# Revit family: Поли-Групп_ЗадвижкаКлиноваяEAZ-EК-F4_DN40-900
name_source: partatom
category: Арматура трубопроводов
units: mm (PartAtom-declared; Revit-internal decimal feet)

## family parameters
Всегда вертикально = Да
На основе рабочей плоскости = Нет
Общий = Нет
При загрузке вырезать с полостями = Нет
Размер круглого соединителя = Использовать диаметр
Тип детали = Клапан - Вставляется

## types (29) — shared parameters
ADSK_URL страницы изделия = https://www.polycorr.ru
ADSK_Версия Revit = 2019
ADSK_Единица измерения = шт
ADSK_Завод-изготовитель = ООО ПК «Поли-Групп»
ADSK_Количество = 1
ADSK_Материал = Высокопрочный чугун GGG-40
ADSK_Материал наименование = Высокопрочный чугун с шаровидным графитом (GGG-40)
Класс герметичности = А по ГОСТ Р 9544-2015
Материал Диска = Высокопрочный чугун с шаровидным графитом (GGG-40)
Материал уплотнителя = EPDM/NBR
Назначение = Для установки в качестве запорного устройства на трубопроводах
Покрытие = Высококачественное эпоксидное покрытие толщиной 300 мкм
Рабочая среда = Питьевая вода, техническая вода, канализационные стоки, морская вода
Разработчик = https://3dbim.pro
Срок службы = 50 лет
ТВ = Поли-Групп_ЗадвижкаКлиноваяEAZ-EК-F4_DN40-900
Температура рабочей среды = 0 до +70°С
Тип привода = Штурвал
Тип присоединения = Фланцевое

## per-type parameters (varying)
- 40-16: A=135 мм; ADSK_Марка=EAZ-GV-4-F4 DN40 PN16; ADSK_Масса=8.2; ADSK_Масса_Текст=8.2; ADSK_Наименование=Задвижка с обрезиненным клином EAZ EK F4 для воды с мягким уплотнением фланцевая маховик DN40 PN16; ADSK_Наименование краткое=Задвижка клиновая EAZ EK F4 DN40 PN16; D=150 мм; D2=88 мм; DN=40 мм; DO=160 мм; D_Наружный=49 мм; H2=240 мм; Kv=0.2 м³/ч; L=140 мм; PN=16.0 бары; R=10 мм; b=19 мм; d1=10 мм; f=3 мм; h2=120 мм; l1=84 мм; l2=91 мм; l3=126 мм; t=12 мм; Габаритные размеры=150х140х315
- 50-16: A=149 мм; ADSK_Марка=EAZ-GV-4-F4 DN50 PN16; ADSK_Масса=9.2; ADSK_Масса_Текст=9.2; ADSK_Наименование=Задвижка с обрезиненным клином EAZ EK F4 для воды с мягким уплотнением фланцевая маховик DN50 PN16; ADSK_Наименование краткое=Задвижка клиновая EAZ EK F4 DN50 PN16; D=165 мм; D2=100 мм; DN=50 мм; DO=160 мм; D_Наружный=59 мм; H2=240 мм; Kv=0.2 м³/ч; L=150 мм; PN=16.0 бары; R=10 мм; b=19 мм; d1=13 мм; f=3 мм; h2=120 мм; l1=90 мм; l2=98 мм; l3=135 мм; t=12 мм; Габаритные размеры=165х150х323
- 65-16: A=167 мм; ADSK_Марка=EAZ-GV-4-F4 DN65 PN16; ADSK_Масса=12; ADSK_Масса_Текст=12; ADSK_Наименование=Задвижка с обрезиненным клином EAZ EK F4 для воды с мягким уплотнением фланцевая маховик DN65 PN16; ADSK_Наименование краткое=Задвижка клиновая EAZ EK F4 DN65 PN16; D=185 мм; D2=120 мм; DN=65 мм; DO=160 мм; D_Наружный=74 мм; H2=259 мм; Kv=0.2 м³/ч; L=170 мм; PN=16.0 бары; R=10 мм; b=19 мм; d1=16 мм; f=3 мм; h2=130 мм; l1=102 мм; l2=111 мм; l3=153 мм; t=13 мм; Габаритные размеры=185х170х352
- 80-16: A=180 мм; ADSK_Марка=EAZ-GV-4-F4 DN80 PN16; ADSK_Масса=14; ADSK_Масса_Текст=14; ADSK_Наименование=Задвижка с обрезиненным клином EAZ EK F4 для воды с мягким уплотнением фланцевая маховик DN80 PN16; ADSK_Наименование краткое=Задвижка клиновая EAZ EK F4 DN80 PN16; D=200 мм; D2=135 мм; DN=80 мм; DO=200 мм; D_Наружный=89 мм; H2=295 мм; Kv=0.1 м³/ч; L=180 мм; PN=16.0 бары; R=10 мм; b=19 мм; d1=20 мм; f=3 мм; h2=148 мм; l1=108 мм; l2=117 мм; l3=162 мм; t=15 мм; Габаритные размеры=200х180х395
- 100-16: A=198 мм; ADSK_Марка=EAZ-GV-4-F4 DN100 PN16; ADSK_Масса=18; ADSK_Масса_Текст=18; ADSK_Наименование=Задвижка с обрезиненным клином EAZ EK F4 для воды с мягким уплотнением фланцевая маховик DN100 PN16; ADSK_Наименование краткое=Задвижка клиновая EAZ EK F4 DN100 PN16; D=220 мм; D2=156 мм; DN=100 мм; DO=200 мм; D_Наружный=109 мм; H2=327 мм; Kv=0.1 м³/ч; L=190 мм; PN=16.0 бары; R=11 мм; b=19 мм; d1=25 мм; f=3 мм; h2=164 мм; l1=114 мм; l2=124 мм; l3=171 мм; t=16 мм; Габаритные размеры=220х190х437
- 125-16: A=225 мм; ADSK_Марка=EAZ-GV-4-F4 DN125 PN16; ADSK_Масса=24; ADSK_Масса_Текст=24; ADSK_Наименование=Задвижка с обрезиненным клином EAZ EK F4 для воды с мягким уплотнением фланцевая маховик DN125 PN16; ADSK_Наименование краткое=Задвижка клиновая EAZ EK F4 DN125 PN16; D=250 мм; D2=186 мм; DN=125 мм; DO=250 мм; D_Наружный=134 мм; H2=388 мм; Kv=0.1 м³/ч; L=200 мм; PN=16.0 бары; R=11 мм; b=19 мм; d1=31 мм; f=3 мм; h2=194 мм; l1=120 мм; l2=130 мм; l3=180 мм; t=19 мм; Габаритные размеры=250х200х513
- 150-16: A=257 мм; ADSK_Марка=EAZ-GV-4-F4 DN150 PN16; ADSK_Масса=31; ADSK_Масса_Текст=31; ADSK_Наименование=Задвижка с обрезиненным клином EAZ EK F4 для воды с мягким уплотнением фланцевая маховик DN150 PN16; ADSK_Наименование краткое=Задвижка клиновая EAZ EK F4 DN150 PN16; D=285 мм; D2=212 мм; DN=150 мм; DO=250 мм; D_Наружный=159 мм; H2=431 мм; Kv=0.1 м³/ч; L=210 мм; PN=16.0 бары; R=11 мм; b=19 мм; d1=38 мм; f=3 мм; h2=216 мм; l1=126 мм; l2=137 мм; l3=189 мм; t=22 мм; Габаритные размеры=285х210х574
- 200-16: A=306 мм; ADSK_Марка=EAZ-GV-4-F4 DN200 PN16; ADSK_Масса=50; ADSK_Масса_Текст=50; ADSK_Наименование=Задвижка с обрезиненным клином EAZ EK F4 для воды с мягким уплотнением фланцевая маховик DN200 PN16; ADSK_Наименование краткое=Задвижка клиновая EAZ EK F4 DN200 PN16; D=340 мм; D2=268 мм; DN=200 мм; DO=280 мм; D_Наружный=209 мм; H2=527 мм; Kv=0.1 м³/ч; L=230 мм; PN=16.0 бары; R=13 мм; b=20 мм; d1=50 мм; f=3 мм; h2=264 мм; l1=138 мм; l2=150 мм; l3=207 мм; t=26 мм; Габаритные размеры=340х230х697
- 250-16: A=365 мм; ADSK_Марка=EAZ-GV-4-F4 DN250 PN16; ADSK_Масса=77; ADSK_Масса_Текст=77; ADSK_Наименование=Задвижка с обрезиненным клином EAZ EK F4 для воды с мягким уплотнением фланцевая маховик DN250 PN16; ADSK_Наименование краткое=Задвижка клиновая EAZ EK F4 DN250 PN16; D=405 мм; D2=318 мм; DN=250 мм; DO=320 мм; D_Наружный=259 мм; H2=609 мм; Kv=0.1 м³/ч; L=250 мм; PN=16.0 бары; R=15 мм; b=22 мм; d1=63 мм; f=3 мм; h2=305 мм; l1=150 мм; l2=163 мм; l3=225 мм; t=30 мм; Габаритные размеры=405х250х812
- 300-16: A=414 мм; ADSK_Марка=EAZ-GV-4-F4 DN300 PN16; ADSK_Масса=107; ADSK_Масса_Текст=107; ADSK_Наименование=Задвижка с обрезиненным клином EAZ EK F4 для воды с мягким уплотнением фланцевая маховик DN300 PN16; ADSK_Наименование краткое=Задвижка клиновая EAZ EK F4 DN300 PN16; D=460 мм; D2=373 мм; DN=300 мм; DO=350 мм; D_Наружный=309 мм; H2=698 мм; Kv=0.1 м³/ч; L=270 мм; PN=16.0 бары; R=17 мм; b=25 мм; d1=75 мм; f=3 мм; h2=349 мм; l1=162 мм; l2=176 мм; l3=243 мм; t=35 мм; Габаритные размеры=460х270х928
- 350-16: A=468 мм; ADSK_Марка=EAZ-GV-4-F4 DN350 PN16; ADSK_Масса=183; ADSK_Масса_Текст=183; ADSK_Наименование=Задвижка с обрезиненным клином EAZ EK F4 для воды с мягким уплотнением фланцевая маховик DN350 PN16; ADSK_Наименование краткое=Задвижка клиновая EAZ EK F4 DN350 PN16; D=520 мм; D2=433 мм; DN=350 мм; DO=400 мм; D_Наружный=359 мм; H2=796 мм; Kv=0.0 м³/ч; L=290 мм; PN=16.0 бары; R=21 мм; b=27 мм; d1=88 мм; f=3 мм; h2=398 мм; l1=174 мм; l2=189 мм; l3=261 мм; t=40 мм; Габаритные размеры=520х290х1056
- 400-16: A=522 мм; ADSK_Марка=EAZ-GV-4-F4 DN400 PN16; ADSK_Масса=228; ADSK_Масса_Текст=228; ADSK_Наименование=Задвижка с обрезиненным клином EAZ EK F4 для воды с мягким уплотнением фланцевая маховик DN400 PN16; ADSK_Наименование краткое=Задвижка клиновая EAZ EK F4 DN400 PN16; D=580 мм; D2=483 мм; DN=400 мм; DO=500 мм; D_Наружный=409 мм; H2=943 мм; Kv=0.0 м³/ч; L=310 мм; PN=16.0 бары; R=21 мм; b=28 мм; d1=100 мм; f=4 мм; h2=472 мм; l1=186 мм; l2=202 мм; l3=279 мм; t=47 мм; Габаритные размеры=580х310х1233
- 450-16: A=576 мм; ADSK_Марка=EAZ-GV-4-F4 DN450 PN16; ADSK_Масса=320; ADSK_Масса_Текст=320; ADSK_Наименование=Задвижка с обрезиненным клином EAZ EK F4 для воды с мягким уплотнением фланцевая маховик DN450 PN16; ADSK_Наименование краткое=Задвижка клиновая EAZ EK F4 DN450 PN16; D=640 мм; D2=546 мм; DN=450 мм; DO=500 мм; D_Наружный=459 мм; H2=1032 мм; Kv=0.0 м³/ч; L=330 мм; PN=16.0 бары; R=28 мм; b=30 мм; d1=113 мм; f=4 мм; h2=516 мм; l1=198 мм; l2=215 мм; l3=297 мм; t=52 мм; Габаритные размеры=640х330х1352
- 500-16: A=644 мм; ADSK_Марка=EAZ-GV-4-F4 DN500 PN16; ADSK_Масса=394; ADSK_Масса_Текст=394; ADSK_Наименование=Задвижка с обрезиненным клином EAZ EK F4 для воды с мягким уплотнением фланцевая маховик DN500 PN16; ADSK_Наименование краткое=Задвижка клиновая EAZ EK F4 DN500 PN16; D=715 мм; D2=605 мм; DN=500 мм; DO=500 мм; D_Наружный=509 мм; H2=1114 мм; Kv=1.0 м³/ч; L=350 мм; PN=16.0 бары; R=28 мм; b=32 мм; d1=125 мм; f=4 мм; h2=557 мм; l1=210 мм; l2=228 мм; l3=315 мм; t=56 мм; Габаритные размеры=715х350х1472
- 600-16: A=756 мм; ADSK_Марка=EAZ-GV-4-F4 DN600 PN16; ADSK_Масса=580; ADSK_Масса_Текст=580; ADSK_Наименование=Задвижка с обрезиненным клином EAZ EK F4 для воды с мягким уплотнением фланцевая маховик DN600 PN16; ADSK_Наименование краткое=Задвижка клиновая EAZ EK F4 DN600 PN16; D=840 мм; D2=710 мм; DN=600 мм; DO=600 мм; D_Наружный=609 мм; H2=1259 мм; Kv=1.0 м³/ч; L=390 мм; PN=16.0 бары; R=28 мм; b=36 мм; d1=150 мм; f=5 мм; h2=630 мм; l1=234 мм; l2=254 мм; l3=351 мм; t=63 мм; Габаритные размеры=840х390х1679
- 700-16: A=819 мм; ADSK_Марка=EAZ-GV-4-F4 DN700 PN16; ADSK_Масса=1050; ADSK_Масса_Текст=1050; ADSK_Наименование=Задвижка с обрезиненным клином EAZ EK F4 для воды с мягким уплотнением фланцевая маховик DN700 PN16; ADSK_Наименование краткое=Задвижка клиновая EAZ EK F4 DN700 PN16; D=910 мм; D2=797 мм; DN=700 мм; DO=700 мм; D_Наружный=709 мм; H2=1492 мм; Kv=1.0 м³/ч; L=430 мм; PN=16.0 бары; R=31 мм; b=40 мм; d1=175 мм; f=5 мм; h2=746 мм; l1=258 мм; l2=280 мм; l3=387 мм; t=75 мм; Габаритные размеры=910х430х1947
- 800-16: A=923 мм; ADSK_Марка=EAZ-GV-4-F4 DN800 PN16; ADSK_Масса=1250; ADSK_Масса_Текст=1250; ADSK_Наименование=Задвижка с обрезиненным клином EAZ EK F4 для воды с мягким уплотнением фланцевая маховик DN800 PN16; ADSK_Наименование краткое=Задвижка клиновая EAZ EK F4 DN800 PN16; D=1025 мм; D2=909 мм; DN=800 мм; DO=800 мм; D_Наружный=809 мм; H2=1630 мм; Kv=1.0 м³/ч; L=470 мм; PN=16.0 бары; R=33 мм; b=43 мм; d1=200 мм; f=5 мм; h2=815 мм; l1=282 мм; l2=306 мм; l3=423 мм; t=82 мм; Габаритные размеры=1025х470х2143
- 900-16: A=1004 мм; ADSK_Марка=EAZ-GV-4-F4 DN900 PN16; ADSK_Масса=1980; ADSK_Масса_Текст=1980; ADSK_Наименование=Задвижка с обрезиненным клином EAZ EK F4 для воды с мягким уплотнением фланцевая маховик DN900 PN16; ADSK_Наименование краткое=Задвижка клиновая EAZ EK F4 DN900 PN16; D=1115 мм; D2=1001 мм; DN=900 мм; DO=800 мм; D_Наружный=909 мм; H2=2018 мм; Kv=1.0 м³/ч; L=510 мм; PN=16.0 бары; R=37 мм; b=47 мм; d1=225 мм; f=5 мм; h2=1009 мм; l1=306 мм; l2=332 мм; l3=459 мм; t=101 мм; Габаритные размеры=1115х510х2576
- 200-10: A=306 мм; ADSK_Марка=EAZ-GV-4-F4 DN200 PN10; ADSK_Масса=50; ADSK_Масса_Текст=50; ADSK_Наименование=Задвижка с обрезиненным клином EAZ EK F4 для воды с мягким уплотнением фланцевая маховик DN200 PN10; ADSK_Наименование краткое=Задвижка клиновая EAZ EK F4 DN200 PN10; D=340 мм; D2=268 мм; DN=200 мм; DO=280 мм; D_Наружный=209 мм; H2=527 мм; Kv=0.1 м³/ч; L=230 мм; PN=10.0 бары; R=13 мм; b=20 мм; d1=50 мм; f=3 мм; h2=264 мм; l1=138 мм; l2=150 мм; l3=207 мм; t=26 мм; Габаритные размеры=340х230х697
- 250-10: A=365 мм; ADSK_Марка=EAZ-GV-4-F4 DN250 PN10; ADSK_Масса=77; ADSK_Масса_Текст=77; ADSK_Наименование=Задвижка с обрезиненным клином EAZ EK F4 для воды с мягким уплотнением фланцевая маховик DN250 PN10; ADSK_Наименование краткое=Задвижка клиновая EAZ EK F4 DN250 PN10; D=405 мм; D2=318 мм; DN=250 мм; DO=320 мм; D_Наружный=259 мм; H2=609 мм; Kv=0.1 м³/ч; L=250 мм; PN=10.0 бары; R=15 мм; b=22 мм; d1=63 мм; f=3 мм; h2=305 мм; l1=150 мм; l2=163 мм; l3=225 мм; t=30 мм; Габаритные размеры=405х250х812
- 300-10: A=414 мм; ADSK_Марка=EAZ-GV-4-F4 DN300 PN10; ADSK_Масса=107; ADSK_Масса_Текст=107; ADSK_Наименование=Задвижка с обрезиненным клином EAZ EK F4 для воды с мягким уплотнением фланцевая маховик DN300 PN10; ADSK_Наименование краткое=Задвижка клиновая EAZ EK F4 DN300 PN10; D=460 мм; D2=370 мм; DN=300 мм; DO=350 мм; D_Наружный=309 мм; H2=698 мм; Kv=0.1 м³/ч; L=270 мм; PN=10.0 бары; R=17 мм; b=25 мм; d1=75 мм; f=3 мм; h2=349 мм; l1=162 мм; l2=176 мм; l3=243 мм; t=35 мм; Габаритные размеры=460х270х928
- 350-10: A=468 мм; ADSK_Марка=EAZ-GV-4-F4 DN350 PN10; ADSK_Масса=183; ADSK_Масса_Текст=183; ADSK_Наименование=Задвижка с обрезиненным клином EAZ EK F4 для воды с мягким уплотнением фланцевая маховик DN350 PN10; ADSK_Наименование краткое=Задвижка клиновая EAZ EK F4 DN350 PN10; D=520 мм; D2=430 мм; DN=350 мм; DO=400 мм; D_Наружный=359 мм; H2=796 мм; Kv=0.0 м³/ч; L=290 мм; PN=10.0 бары; R=21 мм; b=27 мм; d1=88 мм; f=3 мм; h2=398 мм; l1=174 мм; l2=189 мм; l3=261 мм; t=40 мм; Габаритные размеры=520х290х1056
- 400-10: A=522 мм; ADSK_Марка=EAZ-GV-4-F4 DN400 PN10; ADSK_Масса=228; ADSK_Масса_Текст=228; ADSK_Наименование=Задвижка с обрезиненным клином EAZ EK F4 для воды с мягким уплотнением фланцевая маховик DN400 PN10; ADSK_Наименование краткое=Задвижка клиновая EAZ EK F4 DN400 PN10; D=580 мм; D2=480 мм; DN=400 мм; DO=500 мм; D_Наружный=409 мм; H2=943 мм; Kv=0.0 м³/ч; L=310 мм; PN=10.0 бары; R=21 мм; b=28 мм; d1=100 мм; f=4 мм; h2=472 мм; l1=186 мм; l2=202 мм; l3=279 мм; t=47 мм; Габаритные размеры=580х310х1233
- 450-10: A=576 мм; ADSK_Марка=EAZ-GV-4-F4 DN450 PN10; ADSK_Масса=320; ADSK_Масса_Текст=320; ADSK_Наименование=Задвижка с обрезиненным клином EAZ EK F4 для воды с мягким уплотнением фланцевая маховик DN450 PN10; ADSK_Наименование краткое=Задвижка клиновая EAZ EK F4 DN450 PN10; D=640 мм; D2=528 мм; DN=450 мм; DO=500 мм; D_Наружный=459 мм; H2=1032 мм; Kv=0.0 м³/ч; L=330 мм; PN=10.0 бары; R=28 мм; b=30 мм; d1=113 мм; f=4 мм; h2=516 мм; l1=198 мм; l2=215 мм; l3=297 мм; t=52 мм; Габаритные размеры=640х330х1352
- 500-10: A=644 мм; ADSK_Марка=EAZ-GV-4-F4 DN500 PN10; ADSK_Масса=394; ADSK_Масса_Текст=394; ADSK_Наименование=Задвижка с обрезиненным клином EAZ EK F4 для воды с мягким уплотнением фланцевая маховик DN500 PN10; ADSK_Наименование краткое=Задвижка клиновая EAZ EK F4 DN500 PN10; D=715 мм; D2=582 мм; DN=500 мм; DO=500 мм; D_Наружный=509 мм; H2=1114 мм; Kv=1.0 м³/ч; L=350 мм; PN=10.0 бары; R=28 мм; b=32 мм; d1=125 мм; f=4 мм; h2=557 мм; l1=210 мм; l2=228 мм; l3=315 мм; t=56 мм; Габаритные размеры=715х350х1472
- 600-10: A=756 мм; ADSK_Марка=EAZ-GV-4-F4 DN600 PN10; ADSK_Масса=580; ADSK_Масса_Текст=580; ADSK_Наименование=Задвижка с обрезиненным клином EAZ EK F4 для воды с мягким уплотнением фланцевая маховик DN600 PN10; ADSK_Наименование краткое=Задвижка клиновая EAZ EK F4 DN600 PN10; D=840 мм; D2=680 мм; DN=600 мм; DO=600 мм; D_Наружный=609 мм; H2=1259 мм; Kv=1.0 м³/ч; L=390 мм; PN=10.0 бары; R=28 мм; b=36 мм; d1=150 мм; f=5 мм; h2=630 мм; l1=234 мм; l2=254 мм; l3=351 мм; t=63 мм; Габаритные размеры=840х390х1679
- 700-10: A=819 мм; ADSK_Марка=EAZ-GV-4-F4 DN700 PN10; ADSK_Масса=1050; ADSK_Масса_Текст=1050; ADSK_Наименование=Задвижка с обрезиненным клином EAZ EK F4 для воды с мягким уплотнением фланцевая маховик DN700 PN10; ADSK_Наименование краткое=Задвижка клиновая EAZ EK F4 DN700 PN10; D=910 мм; D2=797 мм; DN=700 мм; DO=700 мм; D_Наружный=709 мм; H2=1492 мм; Kv=1.0 м³/ч; L=430 мм; PN=10.0 бары; R=31 мм; b=40 мм; d1=175 мм; f=5 мм; h2=746 мм; l1=258 мм; l2=280 мм; l3=387 мм; t=75 мм; Габаритные размеры=910х430х1947
- 800-10: A=923 мм; ADSK_Марка=EAZ-GV-4-F4 DN800 PN10; ADSK_Масса=1250; ADSK_Масса_Текст=1250; ADSK_Наименование=Задвижка с обрезиненным клином EAZ EK F4 для воды с мягким уплотнением фланцевая маховик DN800 PN10; ADSK_Наименование краткое=Задвижка клиновая EAZ EK F4 DN800 PN10; D=1025 мм; D2=909 мм; DN=800 мм; DO=800 мм; D_Наружный=809 мм; H2=1630 мм; Kv=1.0 м³/ч; L=470 мм; PN=10.0 бары; R=33 мм; b=43 мм; d1=200 мм; f=5 мм; h2=815 мм; l1=282 мм; l2=306 мм; l3=423 мм; t=82 мм; Габаритные размеры=1025х470х2143
- 900-10: A=1004 мм; ADSK_Марка=EAZ-GV-4-F4 DN900 PN10; ADSK_Масса=1980; ADSK_Масса_Текст=1980; ADSK_Наименование=Задвижка с обрезиненным клином EAZ EK F4 для воды с мягким уплотнением фланцевая маховик DN900 PN10; ADSK_Наименование краткое=Задвижка клиновая EAZ EK F4 DN900 PN10; D=1115 мм; D2=1001 мм; DN=900 мм; DO=800 мм; D_Наружный=909 мм; H2=2018 мм; Kv=1.0 м³/ч; L=510 мм; PN=10.0 бары; R=37 мм; b=47 мм; d1=225 мм; f=5 мм; h2=1009 мм; l1=306 мм; l2=332 мм; l3=459 мм; t=101 мм; Габаритные размеры=1115х510х2576
